# Revit family: Legrand - Enveloppes de distribution XL³ S 4000 Gaine à câbles L350xH2200
name_source: partatom
category: Equipement électrique
units: mm (PartAtom-declared; Revit-internal decimal feet)

## family parameters
Basée sur le plan de construction = Non
Configuration du panneau = Deux colonnes, circuits au sein
Cote de connecteur circulaire = Utiliser le diamètre
Couper avec des vides une fois chargée = Non
Numéro OmniClass = 23.80.30.11.17
Partagée = Non
Point de calcul de pièce = Non
Titre OmniClass = Distribution Boards and Control Panels
Toujours verticalement = Oui
Type d'élément = Tableau de raccordement

## types (3) — shared parameters
Conditions Générale d'Utilisation = https://export.legrand.com
ETIM Class 6.0 = EC000261
Fabricant = Legrand
IK = 07
IP = 40
Matière = Acier
RAL = 9003
URL = www.legrand.fr
kit finition = Non
kit finition profondeur 400mm = Non
kit finition profondeur 600mm = Non
kit finition profondeur 800mm = Non
panneau arrière = Oui
panneau droit = Oui
panneau gauche = Oui
porte = Oui
socle 100mm = Non
socle 200mm = Non
socle profondeur 400mm = Non
socle profondeur 400mm Hauteur 200mm = Non
socle profondeur 600mm = Non
socle profondeur 600mm Hauteur 200mm = Non
socle profondeur 800mm = Non
socle profondeur 800mm Hauteur 200mm = Non
zero-valued in all types: Elévation par défaut, Hauteur _socle

## per-type parameters (varying)
| type | Description | panneau latéral droit profondeur 400mm | panneau latéral droit profondeur 600mm | panneau latéral droit profondeur 800mm | panneau latéral gauche profondeur 400mm | panneau latéral gauche profondeur 600mm | panneau latéral gauche profondeur 800mm | porte profondeur 400mm | porte profondeur 600mm | porte profondeur 800mm | profondeur 400mm | profondeur 600mm | profondeur 800mm | structure 338020 | structure 338024 | structure 338028 |
| XL³ S 4000 - Gaine à câbles - Métal - Hauteur 2200mm - Largeur 350mm - Profondeur 400mm | Ref 338020 + 338080 + 338071 + 338110 - XL³ S 4000 - Gaine à câbles - Métal - Hauteur 2200mm - Largeur 350mm - Profondeur 400mm | Oui | Non | Non | Oui | Non | Non | Oui | Non | Non | Oui | Non | Non | Oui | Non | Non |
| XL³ S 4000 - Gaine à câbles - Métal - Hauteur 2200mm - Largeur 350mm - Profondeur 600mm | Ref 338024 + 338080 + 338072 + 338110 - XL³ S 4000 - Gaine à câbles - Métal - Hauteur 2200mm - Largeur 350mm - Profondeur 600mm | Non | Oui | Non | Non | Oui | Non | Non | Oui | Non | Non | Oui | Non | Non | Oui | Non |
| XL³ S 4000 - Gaine à câbles - Métal - Hauteur 2200mm - Largeur 350mm - Profondeur 800mm | Ref 338028 + 338080 + 338073 + 338110 -XL³ S 4000 - Gaine à câbles - Métal - Hauteur 2200mm - Largeur 350mm - Profondeur 800mm | Non | Non | Oui | Non | Non | Oui | Non | Non | Oui | Non | Non | Oui | Non | Non | Oui |
